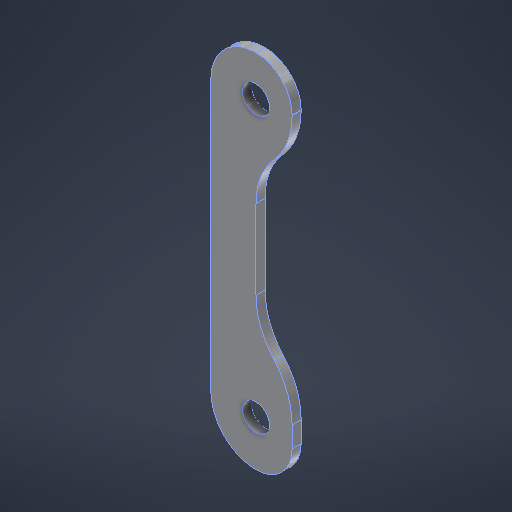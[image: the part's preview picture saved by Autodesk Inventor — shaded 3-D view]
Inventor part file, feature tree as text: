
AUTODESK INVENTOR PART (.ipt)
format: ipt  version: 2025.3 (Build 293356000, 356)  size: 225,280 bytes
history: native  units: in
note: dims shown in document units (in); Inventor stores cm internally (conversion verified against a paired STEP export)
features: fillet x3, extrude x1, sketch x1
ambient origin geometry x8: Origin, YZ Plane, XZ Plane, XY Plane, X Axis, Y Axis, Z Axis, Center Point
bodies: Body1 (feature_tree)
feature tree (5):
  extrude  "Extrusion2"  Depth=0.1575in
  fillet  "Fillet4"  Radius=0.1969in
  fillet  "Fillet6"  Radius=1.5748in
  fillet  "Fillet7"  Radius=0.1772in
  sketch  "Sketch3"  dims[d22=0.0394in d23=0.0in d24=0.1575in d26=0.1969in d27=1.5748in d28=0.1772in d29=0.0984in d32=0.0197in d33=0.3071in]
